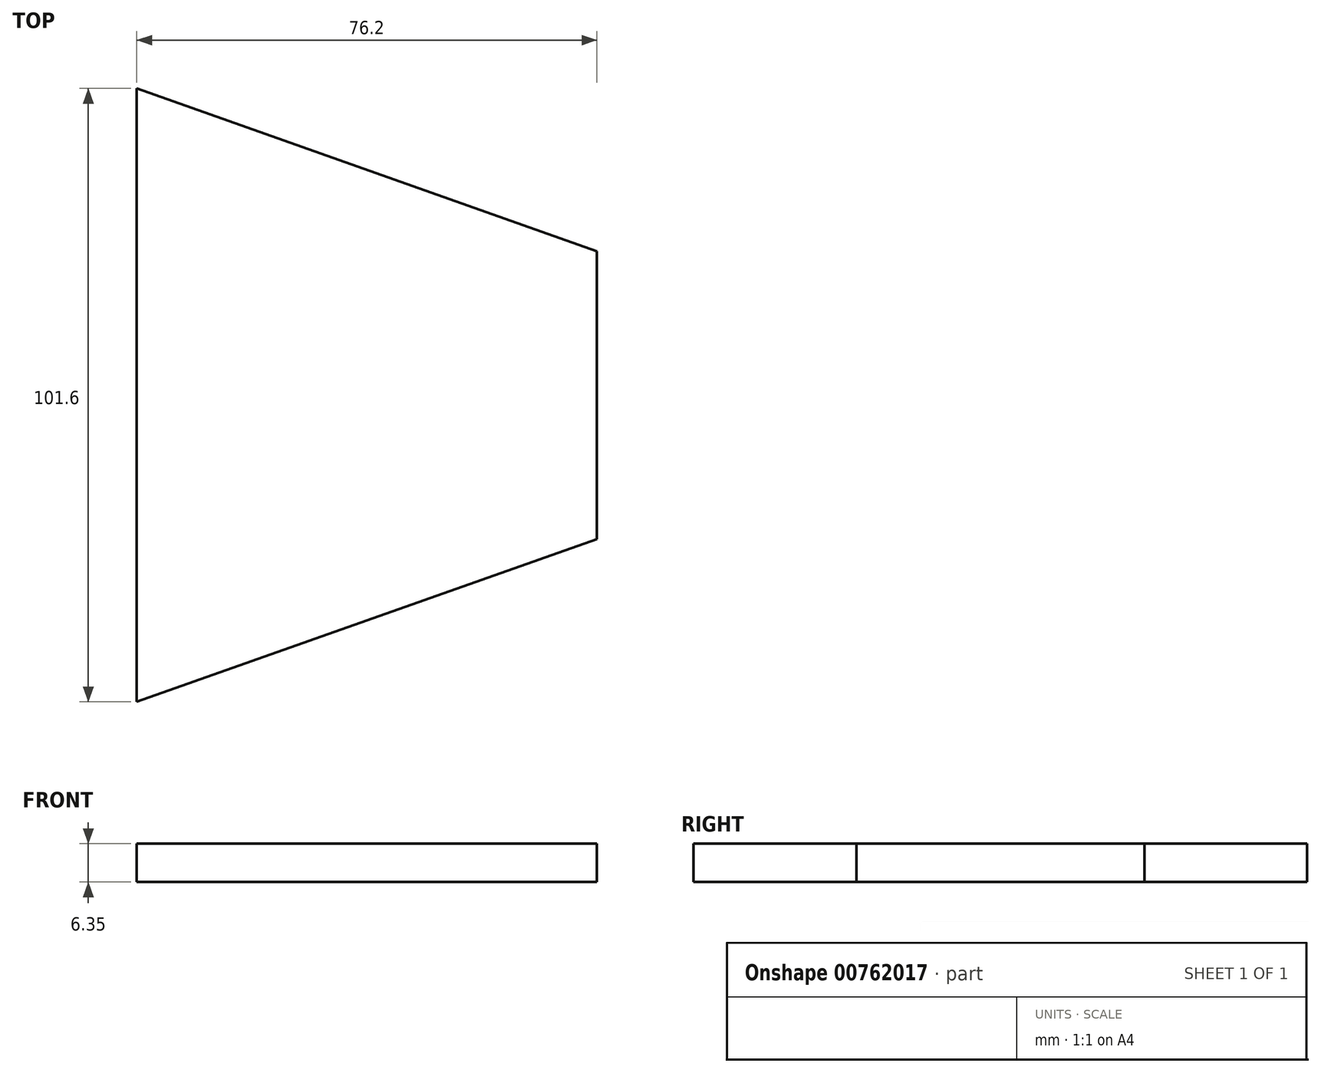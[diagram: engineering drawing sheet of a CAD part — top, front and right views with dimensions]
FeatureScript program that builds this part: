
annotation { "Feature Type Name" : "Feature", "Feature Type Description" : "" }
export const myFeature = defineFeature(function(context is Context, id is Id, definition is map)
    precondition{}
    {
        {
            var Q0;
            Q0=qCreatedBy(makeId("Top.planeOp"),FACE);
            var sketch = newSketch(context, id + "F0", { "sketchPlane" : qUnion([Q0])});
            skLineSegment(sketch, "E0", {"start": v(-113.4, 74.11) * mm, "end": v(-113.4, -27.49) * mm});
            skLineSegment(sketch, "E1", {"start": v(-113.4, 74.11) * mm, "end": v(-37.2, 47.17) * mm});
            skLineSegment(sketch, "E2", {"start": v(-113.4, -27.49) * mm, "end": v(-37.2, -0.55) * mm});
            skLineSegment(sketch, "E3", {"start": v(-37.2, 47.17) * mm, "end": v(-37.2, -0.55) * mm});
            skSolve(sketch);
        }
        {
            var Q0;
            Q0=makeQuery(id+"F0.imprint","IMPRINT",FACE,{"disambiguationData":[TD([[makeQuery(id+"F0.imprint","IMPRINT",EDGE,{"derivedFrom":sQuery(id+"F0.wireOp",EDGE,"E0")}),1.0]])]});
            extrude(context, id + "F1", {"entities" : qUnion([Q0]), "depth" : 6.35 * mm, "offsetDistance" : 25.4 * mm});
        }
    });
